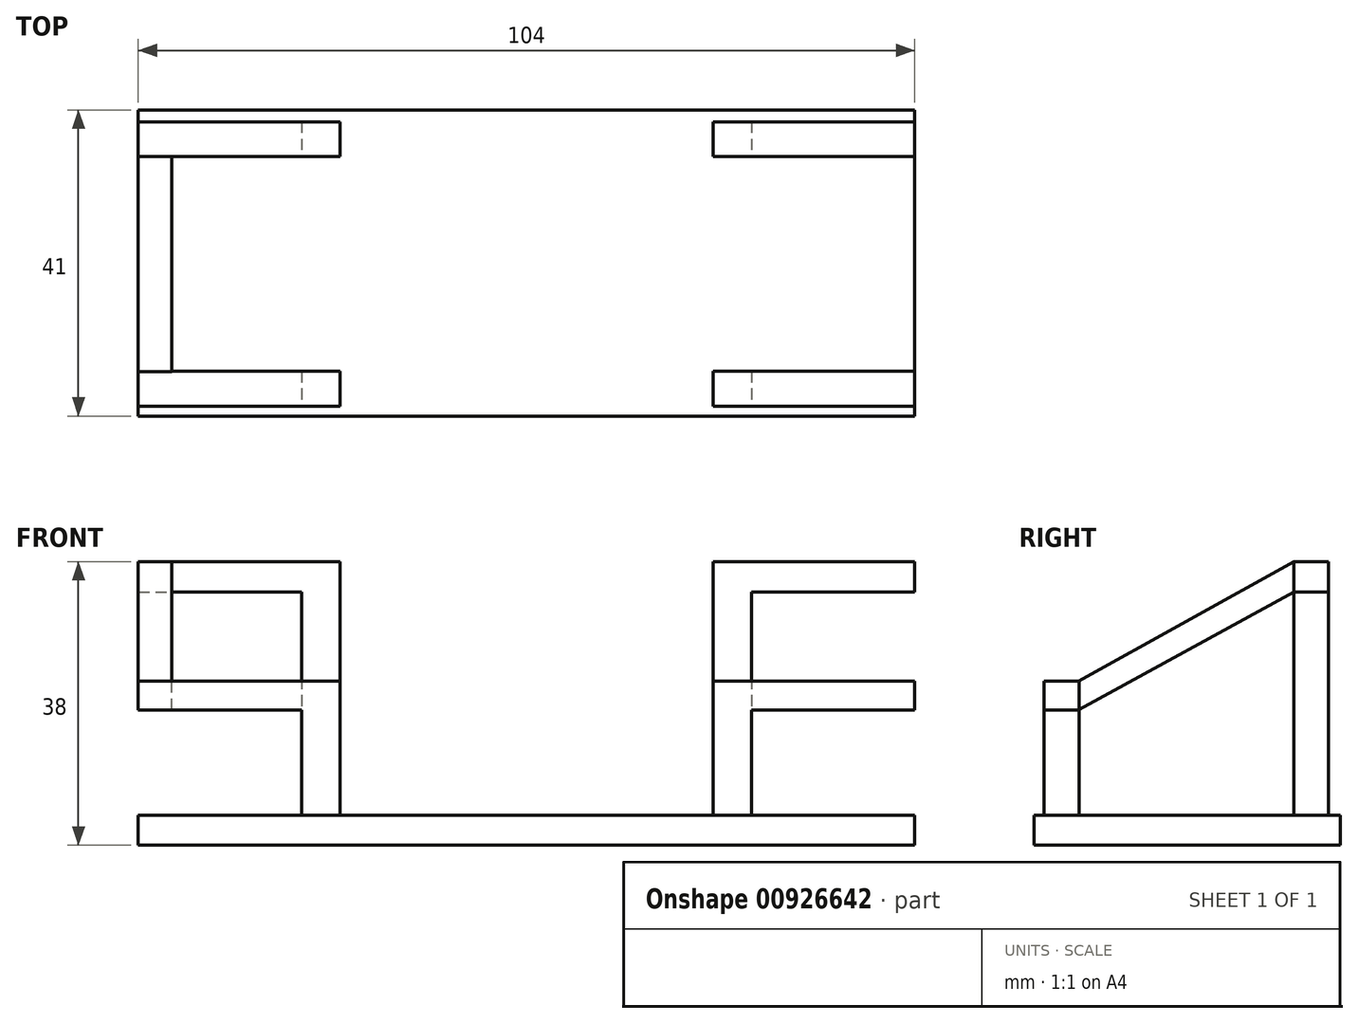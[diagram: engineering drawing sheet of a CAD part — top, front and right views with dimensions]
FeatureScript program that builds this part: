
annotation { "Feature Type Name" : "Feature", "Feature Type Description" : "" }
export const myFeature = defineFeature(function(context is Context, id is Id, definition is map)
    precondition{}
    {
        {
            var Q0;
            Q0=qCreatedBy(makeId("Top.planeOp"),FACE);
            var sketch = newSketch(context, id + "F0", { "sketchPlane" : qUnion([Q0])});
            skLineSegment(sketch, "E0.bottom", {"start": v(-51.15, 21.96) * mm, "end": v(0.85, 21.96) * mm});
            skLineSegment(sketch, "E0.top", {"start": v(-51.15, -19.04) * mm, "end": v(0.85, -19.04) * mm});
            skLineSegment(sketch, "E0.left", {"start": v(-51.15, 21.96) * mm, "end": v(-51.15, -19.04) * mm});
            skLineSegment(sketch, "E0.right", {"start": v(0.85, 21.96) * mm, "end": v(0.85, -19.04) * mm});
            skSolve(sketch);
        }
        {
            var Q0;
            Q0=makeQuery(id+"F0.imprint","IMPRINT",FACE,{"disambiguationData":[TD([[makeQuery(id+"F0.imprint","IMPRINT",EDGE,{"derivedFrom":sQuery(id+"F0.wireOp",EDGE,"E0.bottom")}),-1.0]])]});
            extrude(context, id + "F1", {"entities" : qUnion([Q0]), "depth" : 4 * mm, "offsetDistance" : 25 * mm});
        }
        {
            var Q0;
            Q0=makeQuery(id+"F1.opExtrude","CAP_FACE",FACE,{"disambiguationData":[OSD([sQuery(id+"F0.wireOp",EDGE,"E0.bottom"),sQuery(id+"F0.wireOp",EDGE,"E0.top"),sQuery(id+"F0.wireOp",EDGE,"E0.left"),sQuery(id+"F0.wireOp",EDGE,"E0.right")])],"isStart":false});
            var sketch = newSketch(context, id + "F2", { "sketchPlane" : qUnion([Q0])});
            skLineSegment(sketch, "E1", {"start": v(-29.27, 20.4) * mm, "end": v(-29.27, -17.7) * mm});
            skLineSegment(sketch, "E2", {"start": v(-24.14, 20.4) * mm, "end": v(-24.14, -17.7) * mm});
            skLineSegment(sketch, "E3", {"start": v(-29.27, -17.7) * mm, "end": v(-24.14, -17.7) * mm});
            skLineSegment(sketch, "E4", {"start": v(-24.14, -13.04) * mm, "end": v(-29.27, -13.04) * mm});
            skLineSegment(sketch, "E5", {"start": v(-24.14, 1.35) * mm, "end": v(-26.6, 1.35) * mm});
            skLineSegment(sketch, "E6.MirrorCS", {"start": v(-24.14, 15.73) * mm, "end": v(-29.27, 15.73) * mm});
            skLineSegment(sketch, "E7.MirrorCS", {"start": v(-29.27, 20.4) * mm, "end": v(-24.14, 20.4) * mm});
            skSolve(sketch);
        }
        {
            var Q0;
            {var subQ2=sQuery(id+"F2.wireOp",EDGE,"E6.MirrorCS");Q0=makeQuery(id+"F2.imprint","IMPRINT",FACE,{"disambiguationData":[TD([[makeQuery(id+"F2.imprint","IMPRINT",EDGE,{"derivedFrom":subQ2}),-1.0]])]});}
            extrude(context, id + "F3", {"entities" : qUnion([Q0]), "operationType" : NewBodyOperationType.ADD, "depth" : 34 * mm, "offsetDistance" : 25 * mm});
        }
        {
            var Q0;
            {var subQ0=sQuery(id+"F2.wireOp",EDGE,"E3");Q0=makeQuery(id+"F2.imprint","IMPRINT",FACE,{"disambiguationData":[TD([[makeQuery(id+"F2.imprint","IMPRINT",EDGE,{"derivedFrom":subQ0}),1.0]])]});}
            extrude(context, id + "F4", {"entities" : qUnion([Q0]), "operationType" : NewBodyOperationType.ADD, "depth" : 18 * mm, "offsetDistance" : 25 * mm});
        }
        {
            var Q0;
            Q0=makeQuery(id+"F3.opExtrude","SWEPT_FACE",FACE,{"disambiguationData":[OSD([sQuery(id+"F2.wireOp",EDGE,"E1")])]});
            var sketch = newSketch(context, id + "F5", { "sketchPlane" : qUnion([Q0])});
            skLineSegment(sketch, "E8", {"start": v(-20.4, 33.9) * mm, "end": v(-15.73, 33.9) * mm});
            skSolve(sketch);
        }
        {
            var Q0;
            {var subQ0=sQuery(id+"F5.wireOp",EDGE,"E8");Q0=makeQuery(id+"F5.imprint","IMPRINT",FACE,{"disambiguationData":[TD([[makeQuery(id+"F5.imprint","IMPRINT",EDGE,{"derivedFrom":subQ0}),1.0]])]});}
            extrude(context, id + "F6", {"entities" : qUnion([Q0]), "operationType" : NewBodyOperationType.ADD, "depth" : 21.88 * mm, "offsetDistance" : 25 * mm});
        }
        {
            var Q0;
            Q0=makeQuery(id+"F4.opExtrude","SWEPT_FACE",FACE,{"disambiguationData":[OSD([sQuery(id+"F2.wireOp",EDGE,"E1")])]});
            var sketch = newSketch(context, id + "F7", { "sketchPlane" : qUnion([Q0])});
            skLineSegment(sketch, "E9", {"start": v(13.04, 18.13) * mm, "end": v(17.7, 18.13) * mm});
            skSolve(sketch);
        }
        {
            var Q0;
            {var subQ0=sQuery(id+"F7.wireOp",EDGE,"E9");Q0=makeQuery(id+"F7.imprint","IMPRINT",FACE,{"disambiguationData":[TD([[makeQuery(id+"F7.imprint","IMPRINT",EDGE,{"derivedFrom":subQ0}),1.0]])]});}
            extrude(context, id + "F8", {"entities" : qUnion([Q0]), "operationType" : NewBodyOperationType.ADD, "depth" : 21.88 * mm, "offsetDistance" : 25 * mm});
        }
        {
            var Q0;
            Q0=makeQuery(id+"F6.opExtrude","CAP_FACE",FACE,{"disambiguationData":[OSD([sQuery(id+"F2.wireOp",EDGE,"E1"),sQuery(id+"F2.wireOp",EDGE,"E6.MirrorCS"),sQuery(id+"F2.wireOp",EDGE,"E7.MirrorCS"),sQuery(id+"F5.wireOp",EDGE,"E8")])],"isStart":false});
            var sketch = newSketch(context, id + "F9", { "sketchPlane" : qUnion([Q0])});
            skLineSegment(sketch, "E10", {"start": v(-15.73, 38) * mm, "end": v(14.01, 21.48) * mm});
            skLineSegment(sketch, "E11", {"start": v(-15.73, 33.9) * mm, "end": v(13.03, 18.15) * mm});
            skLineSegment(sketch, "E12", {"start": v(13.03, 18.15) * mm, "end": v(14.01, 18.15) * mm});
            skLineSegment(sketch, "E13", {"start": v(14.01, 18.15) * mm, "end": v(14.01, 21.48) * mm});
            skSolve(sketch);
        }
        {
            var Q0;
            Q0=makeQuery(id+"F9.imprint","IMPRINT",FACE,{"disambiguationData":[TD([[makeQuery(id+"F9.imprint","IMPRINT",EDGE,{"derivedFrom":sQuery(id+"F9.wireOp",EDGE,"E10")}),-1.0]])]});
            extrude(context, id + "F10", {"entities" : qUnion([Q0]), "oppositeDirection" : true, "depth" : 4.5 * mm, "offsetDistance" : 25 * mm});
        }
        {
            var Q0;
            Q0=makeQuery(id+"F1.opExtrude","SWEPT_BODY",BODY,{"disambiguationData":[OSD([sQuery(id+"F0.wireOp",EDGE,"E0.bottom"),sQuery(id+"F0.wireOp",EDGE,"E0.top"),sQuery(id+"F0.wireOp",EDGE,"E0.left"),sQuery(id+"F0.wireOp",EDGE,"E0.right")])]});
            var Q1;
            Q1=makeQuery(id+"F1.opExtrude","SWEPT_FACE",FACE,{"disambiguationData":[OSD([sQuery(id+"F0.wireOp",EDGE,"E0.right")])]});
            mirror(context, id + "F11", {"operationType" : NewBodyOperationType.ADD, "entities" : qUnion([Q0]), "mirrorPlane" : qUnion([Q1])});
        }
    });
